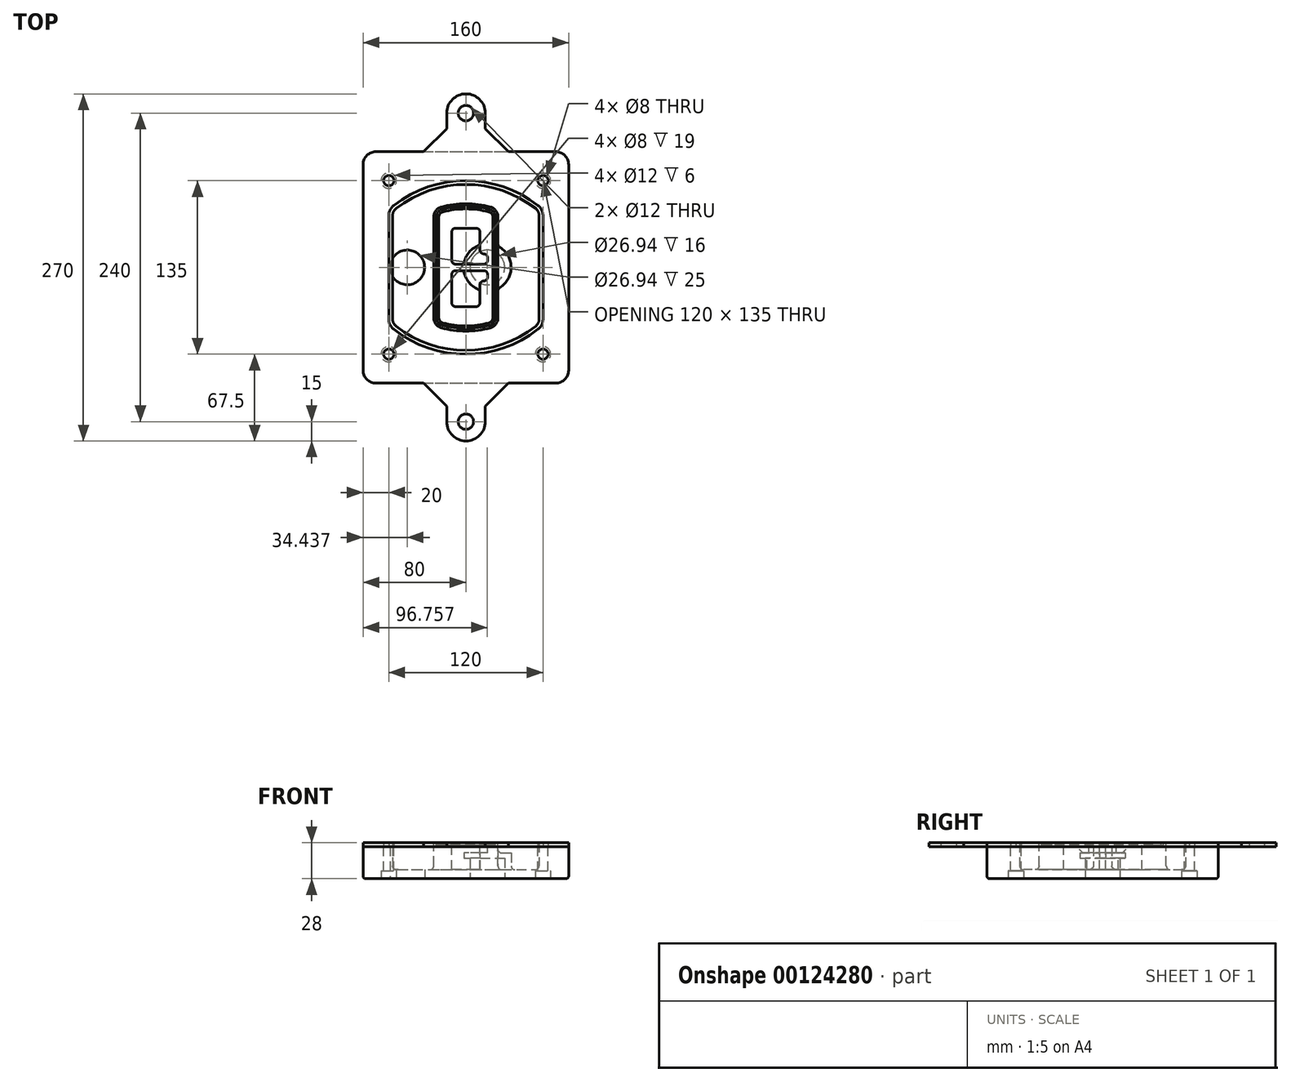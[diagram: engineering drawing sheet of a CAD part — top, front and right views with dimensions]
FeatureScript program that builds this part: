
annotation { "Feature Type Name" : "Feature", "Feature Type Description" : "" }
export const myFeature = defineFeature(function(context is Context, id is Id, definition is map)
    precondition{}
    {
        {
            var Q0;
            Q0=qCreatedBy(makeId("Top.planeOp"),FACE);
            var sketch = newSketch(context, id + "F0", { "sketchPlane" : qUnion([Q0])});
            skPoint(sketch, "E0.rect.middle", {"position": v(0, 0) * mm});
            skLineSegment(sketch, "E1.bottom", {"start": v(-70, -90) * mm, "end": v(70, -90) * mm});
            skLineSegment(sketch, "E1.top", {"start": v(-70, 90) * mm, "end": v(70, 90) * mm});
            skLineSegment(sketch, "E1.left", {"start": v(-80, -80) * mm, "end": v(-80, 80) * mm});
            skLineSegment(sketch, "E1.right", {"start": v(80, -80) * mm, "end": v(80, 80) * mm});
            skLineSegment(sketch, "E2", {"start": v(-80, 90) * mm, "end": v(80, -90) * mm, "construction": true});
            skLineSegment(sketch, "E3", {"start": v(80, 90) * mm, "end": v(-80, -90) * mm, "construction": true});
            skCircle(sketch, "E4", {"center": v(-60, 67.5) * mm, "radius": 4 * mm});
            skCircle(sketch, "E5", {"center": v(60, 67.5) * mm, "radius": 4 * mm});
            skCircle(sketch, "E6", {"center": v(60, -67.5) * mm, "radius": 4 * mm});
            skCircle(sketch, "E7", {"center": v(-60, -67.5) * mm, "radius": 4 * mm});
            skLineSegment(sketch, "E8", {"start": v(-60, 67.5) * mm, "end": v(60, 67.5) * mm, "construction": true});
            skLineSegment(sketch, "E9", {"start": v(60, 67.5) * mm, "end": v(60, -67.5) * mm, "construction": true});
            skLineSegment(sketch, "E10", {"start": v(60, -67.5) * mm, "end": v(-60, -67.5) * mm, "construction": true});
            skLineSegment(sketch, "E11", {"start": v(-60, -67.5) * mm, "end": v(-60, 67.5) * mm, "construction": true});
            skLineSegment(sketch, "E12", {"start": v(-60, 40.3) * mm, "end": v(-60, -40.3) * mm});
            skLineSegment(sketch, "E13", {"start": v(60, 40.3) * mm, "end": v(60, -40.3) * mm});
            skArc(sketch, "E14", {"start": v(56.15, 48.18) * mm, "mid": v(0, 67.5) * mm, "end": v(-56.15, 48.18) * mm});
            skArc(sketch, "E15", {"start": v(-56.15, -48.18) * mm, "mid": v(0, -67.5) * mm, "end": v(56.15, -48.18) * mm});
            skLineSegment(sketch, "E16", {"start": v(-60, 0) * mm, "end": v(60, 0) * mm, "construction": true});
            skPoint(sketch, "E17.visualSharp", {"position": v(-60, -45) * mm});
            skArc(sketch, "E17.filletArc", {"start": v(-60, -40.3) * mm, "mid": v(-58.99, -44.68) * mm, "end": v(-56.15, -48.18) * mm});
            skPoint(sketch, "E18.visualSharp", {"position": v(-60, 45) * mm});
            skArc(sketch, "E18.filletArc", {"start": v(-56.15, 48.18) * mm, "mid": v(-58.99, 44.68) * mm, "end": v(-60, 40.3) * mm});
            skPoint(sketch, "E19.visualSharp", {"position": v(60, 45) * mm});
            skArc(sketch, "E19.filletArc", {"start": v(60, 40.3) * mm, "mid": v(58.99, 44.68) * mm, "end": v(56.15, 48.18) * mm});
            skPoint(sketch, "E20.visualSharp", {"position": v(60, -45) * mm});
            skArc(sketch, "E20.filletArc", {"start": v(56.15, -48.18) * mm, "mid": v(58.99, -44.68) * mm, "end": v(60, -40.3) * mm});
            skPoint(sketch, "E21.visualSharp", {"position": v(-80, 90) * mm});
            skArc(sketch, "E21.filletArc", {"start": v(-70, 90) * mm, "mid": v(-77.07, 87.07) * mm, "end": v(-80, 80) * mm});
            skPoint(sketch, "E22.visualSharp", {"position": v(80, 90) * mm});
            skArc(sketch, "E22.filletArc", {"start": v(80, 80) * mm, "mid": v(77.07, 87.07) * mm, "end": v(70, 90) * mm});
            skPoint(sketch, "E23.visualSharp", {"position": v(80, -90) * mm});
            skArc(sketch, "E23.filletArc", {"start": v(70, -90) * mm, "mid": v(77.07, -87.07) * mm, "end": v(80, -80) * mm});
            skPoint(sketch, "E24.visualSharp", {"position": v(-80, -90) * mm});
            skArc(sketch, "E24.filletArc", {"start": v(-80, -80) * mm, "mid": v(-77.07, -87.07) * mm, "end": v(-70, -90) * mm});
            skArc(sketch, "E25.0", {"start": v(57, 40.3) * mm, "mid": v(56.3, 43.36) * mm, "end": v(54.3, 45.81) * mm});
            skLineSegment(sketch, "E25.1", {"start": v(57, 40.3) * mm, "end": v(57, -40.3) * mm});
            skArc(sketch, "E25.2", {"start": v(54.3, -45.81) * mm, "mid": v(56.3, -43.36) * mm, "end": v(57, -40.3) * mm});
            skArc(sketch, "E25.3", {"start": v(-54.3, -45.81) * mm, "mid": v(0, -64.5) * mm, "end": v(54.3, -45.81) * mm});
            skArc(sketch, "E25.4", {"start": v(-57, -40.3) * mm, "mid": v(-56.3, -43.36) * mm, "end": v(-54.3, -45.81) * mm});
            skArc(sketch, "E25.5", {"start": v(54.3, 45.81) * mm, "mid": v(0, 64.5) * mm, "end": v(-54.3, 45.81) * mm});
            skLineSegment(sketch, "E25.6", {"start": v(-57, 40.3) * mm, "end": v(-57, -40.3) * mm});
            skArc(sketch, "E25.7", {"start": v(-54.3, 45.81) * mm, "mid": v(-56.3, 43.36) * mm, "end": v(-57, 40.3) * mm});
            skArc(sketch, "E26.0", {"start": v(-58.62, 51.33) * mm, "mid": v(-62.58, 46.43) * mm, "end": v(-64, 40.3) * mm});
            skArc(sketch, "E26.1", {"start": v(58.62, 51.33) * mm, "mid": v(0, 71.5) * mm, "end": v(-58.62, 51.33) * mm});
            skArc(sketch, "E26.2", {"start": v(64, 40.3) * mm, "mid": v(62.58, 46.43) * mm, "end": v(58.62, 51.33) * mm});
            skLineSegment(sketch, "E26.3", {"start": v(64, 40.3) * mm, "end": v(64, -40.3) * mm});
            skArc(sketch, "E26.4", {"start": v(58.62, -51.33) * mm, "mid": v(62.58, -46.43) * mm, "end": v(64, -40.3) * mm});
            skLineSegment(sketch, "E26.5", {"start": v(-64, 40.3) * mm, "end": v(-64, -40.3) * mm});
            skArc(sketch, "E26.6", {"start": v(-58.62, -51.33) * mm, "mid": v(0, -71.5) * mm, "end": v(58.62, -51.33) * mm});
            skArc(sketch, "E26.7", {"start": v(-64, -40.3) * mm, "mid": v(-62.58, -46.43) * mm, "end": v(-58.62, -51.33) * mm});
            skSolve(sketch);
        }
        {
            var Q0;
            Q0=makeQuery(id+"F0.imprint","IMPRINT",FACE,{"disambiguationData":[TD([[makeQuery(id+"F0.imprint","IMPRINT",EDGE,{"derivedFrom":sQuery(id+"F0.wireOp",EDGE,"E1.bottom")}),1.0]])]});
            var Q1;
            Q1=makeQuery(id+"F0.imprint","IMPRINT",FACE,{"disambiguationData":[TD([[makeQuery(id+"F0.imprint","IMPRINT",EDGE,{"derivedFrom":sQuery(id+"F0.wireOp",EDGE,"E12")}),1.0]])]});
            var Q2;
            Q2=makeQuery(id+"F0.imprint","IMPRINT",FACE,{"disambiguationData":[TD([[makeQuery(id+"F0.imprint","IMPRINT",EDGE,{"derivedFrom":sQuery(id+"F0.wireOp",EDGE,"E25.0")}),1.0]])]});
            var Q3;
            Q3=makeQuery(id+"F0.imprint","IMPRINT",FACE,{"disambiguationData":[TD([[makeQuery(id+"F0.imprint","IMPRINT",EDGE,{"derivedFrom":sQuery(id+"F0.wireOp",EDGE,"E12")}),-1.0]])]});
            extrude(context, id + "F1", {"entities" : qUnion([Q0, Q1, Q2, Q3]), "oppositeDirection" : true, "depth" : 25 * mm});
        }
        {
            var Q0;
            Q0=makeQuery(id+"F0.imprint","IMPRINT",FACE,{"disambiguationData":[TD([[makeQuery(id+"F0.imprint","IMPRINT",EDGE,{"derivedFrom":sQuery(id+"F0.wireOp",EDGE,"E12")}),1.0]])]});
            extrude(context, id + "F2", {"entities" : qUnion([Q0]), "operationType" : NewBodyOperationType.ADD, "depth" : 3 * mm});
        }
        {
            var Q0;
            Q0=makeQuery(id+"F0.imprint","IMPRINT",FACE,{"disambiguationData":[TD([[makeQuery(id+"F0.imprint","IMPRINT",EDGE,{"derivedFrom":sQuery(id+"F0.wireOp",EDGE,"E25.0")}),1.0]])]});
            extrude(context, id + "F3", {"entities" : qUnion([Q0]), "operationType" : NewBodyOperationType.REMOVE, "oppositeDirection" : true, "depth" : 18 * mm});
        }
        {
            var Q0;
            Q0=makeQuery(id+"F2.opExtrude","CAP_FACE",FACE,{"disambiguationData":[OSD([sQuery(id+"F0.wireOp",EDGE,"E12"),sQuery(id+"F0.wireOp",EDGE,"E13"),sQuery(id+"F0.wireOp",EDGE,"E14"),sQuery(id+"F0.wireOp",EDGE,"E15"),sQuery(id+"F0.wireOp",EDGE,"E17.filletArc"),sQuery(id+"F0.wireOp",EDGE,"E18.filletArc"),sQuery(id+"F0.wireOp",EDGE,"E19.filletArc"),sQuery(id+"F0.wireOp",EDGE,"E20.filletArc"),sQuery(id+"F0.wireOp",EDGE,"E25.0"),sQuery(id+"F0.wireOp",EDGE,"E25.1"),sQuery(id+"F0.wireOp",EDGE,"E25.2"),sQuery(id+"F0.wireOp",EDGE,"E25.3"),sQuery(id+"F0.wireOp",EDGE,"E25.4"),sQuery(id+"F0.wireOp",EDGE,"E25.5"),sQuery(id+"F0.wireOp",EDGE,"E25.6"),sQuery(id+"F0.wireOp",EDGE,"E25.7")])],"isStart":false});
            var sketch = newSketch(context, id + "F4", { "sketchPlane" : qUnion([Q0])});
            skArc(sketch, "E27.0", {"start": v(-19.08, -46.97) * mm, "mid": v(0, -49.5) * mm, "end": v(19.08, -46.97) * mm});
            skArc(sketch, "E28.0", {"start": v(19.08, 46.97) * mm, "mid": v(0, 49.5) * mm, "end": v(-19.08, 46.97) * mm});
            skLineSegment(sketch, "E29", {"start": v(-25, 39.25) * mm, "end": v(-25, -39.25) * mm});
            skLineSegment(sketch, "E30", {"start": v(25, 39.25) * mm, "end": v(25, -39.25) * mm});
            skLineSegment(sketch, "E31", {"start": v(-25, 45.1) * mm, "end": v(25, 45.1) * mm, "construction": true});
            skLineSegment(sketch, "E32", {"start": v(-25, -45.1) * mm, "end": v(25, -45.1) * mm, "construction": true});
            skPoint(sketch, "E33.visualSharp", {"position": v(-25, 45.1) * mm});
            skArc(sketch, "E33.filletArc", {"start": v(-19.08, 46.97) * mm, "mid": v(-23.35, 44.11) * mm, "end": v(-25, 39.25) * mm});
            skPoint(sketch, "E34.visualSharp", {"position": v(25, 45.1) * mm});
            skArc(sketch, "E34.filletArc", {"start": v(25, 39.25) * mm, "mid": v(23.35, 44.11) * mm, "end": v(19.08, 46.97) * mm});
            skPoint(sketch, "E35.visualSharp", {"position": v(25, -45.1) * mm});
            skArc(sketch, "E35.filletArc", {"start": v(19.08, -46.97) * mm, "mid": v(23.35, -44.11) * mm, "end": v(25, -39.25) * mm});
            skPoint(sketch, "E36.visualSharp", {"position": v(-25, -45.1) * mm});
            skArc(sketch, "E36.filletArc", {"start": v(-25, -39.25) * mm, "mid": v(-23.35, -44.11) * mm, "end": v(-19.08, -46.97) * mm});
            skArc(sketch, "E37.0", {"start": v(54.3, 45.81) * mm, "mid": v(0, 64.5) * mm, "end": v(-54.3, 45.81) * mm});
            skArc(sketch, "E37.1", {"start": v(-54.3, 45.81) * mm, "mid": v(-56.3, 43.36) * mm, "end": v(-57, 40.3) * mm});
            skLineSegment(sketch, "E37.2", {"start": v(-57, 40.3) * mm, "end": v(-57, -40.3) * mm});
            skArc(sketch, "E37.3", {"start": v(-57, -40.3) * mm, "mid": v(-56.3, -43.36) * mm, "end": v(-54.3, -45.81) * mm});
            skArc(sketch, "E37.4", {"start": v(-54.3, -45.81) * mm, "mid": v(0, -64.5) * mm, "end": v(54.3, -45.81) * mm});
            skArc(sketch, "E37.5", {"start": v(54.3, -45.81) * mm, "mid": v(56.3, -43.36) * mm, "end": v(57, -40.3) * mm});
            skLineSegment(sketch, "E37.6", {"start": v(57, 40.3) * mm, "end": v(57, -40.3) * mm});
            skArc(sketch, "E37.7", {"start": v(57, 40.3) * mm, "mid": v(56.3, 43.36) * mm, "end": v(54.3, 45.81) * mm});
            skLineSegment(sketch, "E38.0", {"start": v(23, 39.25) * mm, "end": v(23, -39.25) * mm});
            skArc(sketch, "E38.1", {"start": v(18.56, -45.04) * mm, "mid": v(21.76, -42.9) * mm, "end": v(23, -39.25) * mm});
            skArc(sketch, "E38.2", {"start": v(-18.56, -45.04) * mm, "mid": v(0, -47.5) * mm, "end": v(18.56, -45.04) * mm});
            skArc(sketch, "E38.3", {"start": v(-23, -39.25) * mm, "mid": v(-21.76, -42.9) * mm, "end": v(-18.56, -45.04) * mm});
            skLineSegment(sketch, "E38.4", {"start": v(-23, 39.25) * mm, "end": v(-23, -39.25) * mm});
            skArc(sketch, "E38.5", {"start": v(23, 39.25) * mm, "mid": v(21.76, 42.9) * mm, "end": v(18.56, 45.04) * mm});
            skArc(sketch, "E38.6", {"start": v(-18.56, 45.04) * mm, "mid": v(-21.76, 42.9) * mm, "end": v(-23, 39.25) * mm});
            skArc(sketch, "E38.7", {"start": v(18.56, 45.04) * mm, "mid": v(0, 47.5) * mm, "end": v(-18.56, 45.04) * mm});
            skArc(sketch, "E39.0", {"start": v(21, 39.25) * mm, "mid": v(20.18, 41.68) * mm, "end": v(18.04, 43.1) * mm});
            skLineSegment(sketch, "E39.1", {"start": v(21, 39.25) * mm, "end": v(21, -39.25) * mm});
            skArc(sketch, "E39.2", {"start": v(18.04, -43.1) * mm, "mid": v(20.18, -41.68) * mm, "end": v(21, -39.25) * mm});
            skArc(sketch, "E39.3", {"start": v(-18.04, -43.1) * mm, "mid": v(0, -45.5) * mm, "end": v(18.04, -43.1) * mm});
            skArc(sketch, "E39.4", {"start": v(-21, -39.25) * mm, "mid": v(-20.18, -41.68) * mm, "end": v(-18.04, -43.1) * mm});
            skArc(sketch, "E39.5", {"start": v(18.04, 43.1) * mm, "mid": v(0, 45.5) * mm, "end": v(-18.04, 43.1) * mm});
            skLineSegment(sketch, "E39.6", {"start": v(-21, 39.25) * mm, "end": v(-21, -39.25) * mm});
            skArc(sketch, "E39.7", {"start": v(-18.04, 43.1) * mm, "mid": v(-20.18, 41.68) * mm, "end": v(-21, 39.25) * mm});
            skLineSegment(sketch, "E40", {"start": v(-25, 0) * mm, "end": v(25, 0) * mm, "construction": true});
            skLineSegment(sketch, "E41", {"start": v(-11, 5.5) * mm, "end": v(-11, 27.5) * mm});
            skLineSegment(sketch, "E42", {"start": v(-8, 30.5) * mm, "end": v(8, 30.5) * mm});
            skLineSegment(sketch, "E43", {"start": v(11, 27.5) * mm, "end": v(11, 13.5) * mm});
            skLineSegment(sketch, "E44", {"start": v(14, 10.5) * mm, "end": v(14, 10.5) * mm});
            skLineSegment(sketch, "E45", {"start": v(17, 7.5) * mm, "end": v(17, 5.5) * mm});
            skLineSegment(sketch, "E46", {"start": v(14, 2.5) * mm, "end": v(-8, 2.5) * mm});
            skPoint(sketch, "E47.visualSharp", {"position": v(-11, 30.5) * mm});
            skArc(sketch, "E47.filletArc", {"start": v(-8, 30.5) * mm, "mid": v(-10.12, 29.62) * mm, "end": v(-11, 27.5) * mm});
            skPoint(sketch, "E48.visualSharp", {"position": v(11, 30.5) * mm});
            skArc(sketch, "E48.filletArc", {"start": v(11, 27.5) * mm, "mid": v(10.12, 29.62) * mm, "end": v(8, 30.5) * mm});
            skPoint(sketch, "E49.visualSharp", {"position": v(11, 10.5) * mm});
            skArc(sketch, "E49.filletArc", {"start": v(11, 13.5) * mm, "mid": v(11.88, 11.38) * mm, "end": v(14, 10.5) * mm});
            skPoint(sketch, "E50.visualSharp", {"position": v(17, 10.5) * mm});
            skArc(sketch, "E50.filletArc", {"start": v(17, 7.5) * mm, "mid": v(16.12, 9.62) * mm, "end": v(14, 10.5) * mm});
            skPoint(sketch, "E51.visualSharp", {"position": v(17, 2.5) * mm});
            skArc(sketch, "E51.filletArc", {"start": v(14, 2.5) * mm, "mid": v(16.12, 3.38) * mm, "end": v(17, 5.5) * mm});
            skPoint(sketch, "E52.visualSharp", {"position": v(-11, 2.5) * mm});
            skArc(sketch, "E52.filletArc", {"start": v(-11, 5.5) * mm, "mid": v(-10.12, 3.38) * mm, "end": v(-8, 2.5) * mm});
            skLineSegment(sketch, "E53.0.MirrorCS", {"start": v(14, -2.5) * mm, "end": v(-8, -2.5) * mm});
            skArc(sketch, "E54.0.MirrorCS", {"start": v(-11, -5.5) * mm, "mid": v(-10.12, -3.38) * mm, "end": v(-8, -2.5) * mm});
            skLineSegment(sketch, "E55.0.MirrorCS", {"start": v(-11, -5.5) * mm, "end": v(-11, -27.5) * mm});
            skArc(sketch, "E56.0.MirrorCS", {"start": v(-8, -30.5) * mm, "mid": v(-10.12, -29.62) * mm, "end": v(-11, -27.5) * mm});
            skLineSegment(sketch, "E57.0.MirrorCS", {"start": v(-8, -30.5) * mm, "end": v(8, -30.5) * mm});
            skArc(sketch, "E58.0.MirrorCS", {"start": v(11, -27.5) * mm, "mid": v(10.12, -29.62) * mm, "end": v(8, -30.5) * mm});
            skLineSegment(sketch, "E59.0.MirrorCS", {"start": v(11, -27.5) * mm, "end": v(11, -13.5) * mm});
            skArc(sketch, "E60.0.MirrorCS", {"start": v(11, -13.5) * mm, "mid": v(11.88, -11.38) * mm, "end": v(14, -10.5) * mm});
            skArc(sketch, "E61.0.MirrorCS", {"start": v(17, -7.5) * mm, "mid": v(16.12, -9.62) * mm, "end": v(14, -10.5) * mm});
            skLineSegment(sketch, "E62.0.MirrorCS", {"start": v(17, -7.5) * mm, "end": v(17, -5.5) * mm});
            skArc(sketch, "E63.0.MirrorCS", {"start": v(14, -2.5) * mm, "mid": v(16.12, -3.38) * mm, "end": v(17, -5.5) * mm});
            skSolve(sketch);
        }
        {
            var Q0;
            Q0=makeQuery(id+"F4.imprint","IMPRINT",FACE,{"disambiguationData":[TD([[makeQuery(id+"F4.imprint","IMPRINT",EDGE,{"derivedFrom":sQuery(id+"F4.wireOp",EDGE,"E27.0")}),1.0]])]});
            var Q1;
            Q1=makeQuery(id+"F4.imprint","IMPRINT",FACE,{"disambiguationData":[TD([[makeQuery(id+"F4.imprint","IMPRINT",EDGE,{"derivedFrom":sQuery(id+"F4.wireOp",EDGE,"E38.0")}),-1.0]])]});
            var Q2;
            Q2=makeQuery(id+"F4.imprint","IMPRINT",FACE,{"disambiguationData":[TD([[makeQuery(id+"F4.imprint","IMPRINT",EDGE,{"derivedFrom":sQuery(id+"F4.wireOp",EDGE,"E39.0")}),1.0]])]});
            extrude(context, id + "F5", {"entities" : qUnion([Q0, Q1, Q2]), "operationType" : NewBodyOperationType.ADD, "endBound" : BoundingType.UP_TO_NEXT, "oppositeDirection" : true, "depth" : 25 * mm});
        }
        {
            var Q0;
            Q0=makeQuery(id+"F4.imprint","IMPRINT",FACE,{"disambiguationData":[TD([[makeQuery(id+"F4.imprint","IMPRINT",EDGE,{"derivedFrom":sQuery(id+"F4.wireOp",EDGE,"E38.0")}),-1.0]])]});
            extrude(context, id + "F6", {"entities" : qUnion([Q0]), "operationType" : NewBodyOperationType.REMOVE, "oppositeDirection" : true, "depth" : 2 * mm});
        }
        {
            var Q0;
            Q0=makeQuery(id+"F1.opExtrude","CAP_FACE",FACE,{"disambiguationData":[OSD([sQuery(id+"F0.wireOp",EDGE,"E1.bottom"),sQuery(id+"F0.wireOp",EDGE,"E1.top"),sQuery(id+"F0.wireOp",EDGE,"E1.left"),sQuery(id+"F0.wireOp",EDGE,"E1.right"),sQuery(id+"F0.wireOp",EDGE,"E4"),sQuery(id+"F0.wireOp",EDGE,"E5"),sQuery(id+"F0.wireOp",EDGE,"E6"),sQuery(id+"F0.wireOp",EDGE,"E7"),sQuery(id+"F0.wireOp",EDGE,"E21.filletArc"),sQuery(id+"F0.wireOp",EDGE,"E22.filletArc"),sQuery(id+"F0.wireOp",EDGE,"E23.filletArc"),sQuery(id+"F0.wireOp",EDGE,"E24.filletArc")])],"isStart":false});
            var sketch = newSketch(context, id + "F7", { "sketchPlane" : qUnion([Q0])});
            skCircle(sketch, "E64", {"center": v(16.76, 0) * mm, "radius": 13.47 * mm});
            skCircle(sketch, "E65", {"center": v(-45.56, 0) * mm, "radius": 13.47 * mm});
            skLineSegment(sketch, "E66", {"start": v(80, 0) * mm, "end": v(-80, 0) * mm});
            skCircle(sketch, "E67", {"center": v(16.76, 0) * mm, "radius": 18.47 * mm});
            skCircle(sketch, "E68", {"center": v(60, -67.5) * mm, "radius": 6 * mm});
            skCircle(sketch, "E69", {"center": v(-60, -67.5) * mm, "radius": 6 * mm});
            skCircle(sketch, "E70", {"center": v(-60, 67.5) * mm, "radius": 6 * mm});
            skCircle(sketch, "E71", {"center": v(60, 67.5) * mm, "radius": 6 * mm});
            skSolve(sketch);
        }
        {
            var Q0;
            {var subQ1=sQuery(id+"F7.wireOp",EDGE,"E66");var subQ4=sQuery(id+"F7.wireOp",EDGE,"E64");var subQ6=makeQuery(id+"F7.imprint","INTERSECT",VERTEX,{"disambiguationData":[OD(0.0)],"derivedFrom":[subQ4,subQ1]});Q0=makeQuery(id+"F7.imprint","IMPRINT",FACE,{"disambiguationData":[TD([[makeQuery(id+"F7.imprint","IMPRINT",EDGE,{"disambiguationData":[TD([[subQ6,-1.0]])],"derivedFrom":subQ4}),-1.0]])]});}
            var Q1;
            {var subQ0=sQuery(id+"F7.wireOp",EDGE,"E66");var subQ1=sQuery(id+"F7.wireOp",EDGE,"E64");var subQ3=makeQuery(id+"F7.imprint","INTERSECT",VERTEX,{"disambiguationData":[OD(0.0)],"derivedFrom":[subQ1,subQ0]});Q1=makeQuery(id+"F7.imprint","IMPRINT",FACE,{"disambiguationData":[TD([[makeQuery(id+"F7.imprint","IMPRINT",EDGE,{"disambiguationData":[TD([[subQ3,-1.0]])],"derivedFrom":subQ1}),1.0]])]});}
            var Q2;
            {var subQ0=sQuery(id+"F7.wireOp",EDGE,"E66");var subQ1=sQuery(id+"F7.wireOp",EDGE,"E64");var subQ3=makeQuery(id+"F7.imprint","INTERSECT",VERTEX,{"disambiguationData":[OD(0.0)],"derivedFrom":[subQ1,subQ0]});Q2=makeQuery(id+"F7.imprint","IMPRINT",FACE,{"disambiguationData":[TD([[makeQuery(id+"F7.imprint","IMPRINT",EDGE,{"disambiguationData":[TD([[subQ3,1.0]])],"derivedFrom":subQ1}),1.0]])]});}
            var Q3;
            {var subQ1=sQuery(id+"F7.wireOp",EDGE,"E66");var subQ4=sQuery(id+"F7.wireOp",EDGE,"E64");var subQ6=makeQuery(id+"F7.imprint","INTERSECT",VERTEX,{"disambiguationData":[OD(0.0)],"derivedFrom":[subQ4,subQ1]});Q3=makeQuery(id+"F7.imprint","IMPRINT",FACE,{"disambiguationData":[TD([[makeQuery(id+"F7.imprint","IMPRINT",EDGE,{"disambiguationData":[TD([[subQ6,1.0]])],"derivedFrom":subQ4}),-1.0]])]});}
            extrude(context, id + "F8", {"entities" : qUnion([Q0, Q1, Q2, Q3]), "operationType" : NewBodyOperationType.ADD, "oppositeDirection" : true, "depth" : 20 * mm});
        }
        {
            var Q0;
            {var subQ0=sQuery(id+"F7.wireOp",EDGE,"E66");var subQ1=sQuery(id+"F7.wireOp",EDGE,"E64");var subQ3=makeQuery(id+"F7.imprint","INTERSECT",VERTEX,{"disambiguationData":[OD(0.0)],"derivedFrom":[subQ1,subQ0]});Q0=makeQuery(id+"F7.imprint","IMPRINT",FACE,{"disambiguationData":[TD([[makeQuery(id+"F7.imprint","IMPRINT",EDGE,{"disambiguationData":[TD([[subQ3,-1.0]])],"derivedFrom":subQ1}),1.0]])]});}
            var Q1;
            {var subQ0=sQuery(id+"F7.wireOp",EDGE,"E66");var subQ1=sQuery(id+"F7.wireOp",EDGE,"E64");var subQ3=makeQuery(id+"F7.imprint","INTERSECT",VERTEX,{"disambiguationData":[OD(0.0)],"derivedFrom":[subQ1,subQ0]});Q1=makeQuery(id+"F7.imprint","IMPRINT",FACE,{"disambiguationData":[TD([[makeQuery(id+"F7.imprint","IMPRINT",EDGE,{"disambiguationData":[TD([[subQ3,1.0]])],"derivedFrom":subQ1}),1.0]])]});}
            extrude(context, id + "F9", {"entities" : qUnion([Q0, Q1]), "operationType" : NewBodyOperationType.REMOVE, "oppositeDirection" : true, "depth" : 16 * mm});
        }
        {
            var Q0;
            {var subQ0=sQuery(id+"F7.wireOp",EDGE,"E66");var subQ1=sQuery(id+"F7.wireOp",EDGE,"E65");var subQ3=makeQuery(id+"F7.imprint","INTERSECT",VERTEX,{"disambiguationData":[OD(0.0)],"derivedFrom":[subQ1,subQ0]});Q0=makeQuery(id+"F7.imprint","IMPRINT",FACE,{"disambiguationData":[TD([[makeQuery(id+"F7.imprint","IMPRINT",EDGE,{"disambiguationData":[TD([[subQ3,-1.0]])],"derivedFrom":subQ1}),1.0]])]});}
            var Q1;
            {var subQ0=sQuery(id+"F7.wireOp",EDGE,"E66");var subQ1=sQuery(id+"F7.wireOp",EDGE,"E65");var subQ3=makeQuery(id+"F7.imprint","INTERSECT",VERTEX,{"disambiguationData":[OD(0.0)],"derivedFrom":[subQ1,subQ0]});Q1=makeQuery(id+"F7.imprint","IMPRINT",FACE,{"disambiguationData":[TD([[makeQuery(id+"F7.imprint","IMPRINT",EDGE,{"disambiguationData":[TD([[subQ3,1.0]])],"derivedFrom":subQ1}),1.0]])]});}
            extrude(context, id + "F10", {"entities" : qUnion([Q0, Q1]), "operationType" : NewBodyOperationType.REMOVE, "oppositeDirection" : true, "depth" : 25 * mm});
        }
        {
            var Q0;
            Q0=makeQuery(id+"F7.imprint","IMPRINT",FACE,{"disambiguationData":[TD([[makeQuery(id+"F7.imprint","IMPRINT",EDGE,{"derivedFrom":sQuery(id+"F7.wireOp",EDGE,"E68")}),1.0]])]});
            var Q1;
            Q1=makeQuery(id+"F7.imprint","IMPRINT",FACE,{"disambiguationData":[TD([[makeQuery(id+"F7.imprint","IMPRINT",EDGE,{"derivedFrom":makeQuery(id+"F1.opExtrude","CAP_EDGE",EDGE,{"disambiguationData":[OSD([sQuery(id+"F0.wireOp",EDGE,"E5")])],"isStart":false})}),-1.0]])]});
            var Q2;
            Q2=makeQuery(id+"F7.imprint","IMPRINT",FACE,{"disambiguationData":[TD([[makeQuery(id+"F7.imprint","IMPRINT",EDGE,{"derivedFrom":sQuery(id+"F7.wireOp",EDGE,"E69")}),1.0]])]});
            var Q3;
            Q3=makeQuery(id+"F7.imprint","IMPRINT",FACE,{"disambiguationData":[TD([[makeQuery(id+"F7.imprint","IMPRINT",EDGE,{"derivedFrom":makeQuery(id+"F1.opExtrude","CAP_EDGE",EDGE,{"disambiguationData":[OSD([sQuery(id+"F0.wireOp",EDGE,"E4")])],"isStart":false})}),-1.0]])]});
            var Q4;
            Q4=makeQuery(id+"F7.imprint","IMPRINT",FACE,{"disambiguationData":[TD([[makeQuery(id+"F7.imprint","IMPRINT",EDGE,{"derivedFrom":sQuery(id+"F7.wireOp",EDGE,"E70")}),1.0]])]});
            var Q5;
            Q5=makeQuery(id+"F7.imprint","IMPRINT",FACE,{"disambiguationData":[TD([[makeQuery(id+"F7.imprint","IMPRINT",EDGE,{"derivedFrom":makeQuery(id+"F1.opExtrude","CAP_EDGE",EDGE,{"disambiguationData":[OSD([sQuery(id+"F0.wireOp",EDGE,"E7")])],"isStart":false})}),-1.0]])]});
            var Q6;
            Q6=makeQuery(id+"F7.imprint","IMPRINT",FACE,{"disambiguationData":[TD([[makeQuery(id+"F7.imprint","IMPRINT",EDGE,{"derivedFrom":sQuery(id+"F7.wireOp",EDGE,"E71")}),1.0]])]});
            var Q7;
            Q7=makeQuery(id+"F7.imprint","IMPRINT",FACE,{"disambiguationData":[TD([[makeQuery(id+"F7.imprint","IMPRINT",EDGE,{"derivedFrom":makeQuery(id+"F1.opExtrude","CAP_EDGE",EDGE,{"disambiguationData":[OSD([sQuery(id+"F0.wireOp",EDGE,"E6")])],"isStart":false})}),-1.0]])]});
            extrude(context, id + "F11", {"entities" : qUnion([Q0, Q1, Q2, Q3, Q4, Q5, Q6, Q7]), "operationType" : NewBodyOperationType.REMOVE, "oppositeDirection" : true, "depth" : 6 * mm});
        }
        {
            var Q0;
            Q0=makeQuery(id+"F9.boolean.opBoolean","COPY",FACE,{"derivedFrom":makeQuery(id+"F9.opExtrude","CAP_FACE",FACE,{"disambiguationData":[OSD([sQuery(id+"F7.wireOp",EDGE,"E64")])],"isStart":false})});
            var sketch = newSketch(context, id + "F12", { "sketchPlane" : qUnion([Q0])});
            skArc(sketch, "E72.0", {"start": v(11, 17.55) * mm, "mid": v(2.57, 11.82) * mm, "end": v(-1.54, 2.5) * mm});
            skArc(sketch, "E72.1", {"start": v(-1.54, -2.5) * mm, "mid": v(2.57, -11.82) * mm, "end": v(11, -17.55) * mm});
            skLineSegment(sketch, "E73", {"start": v(-1.54, -2.5) * mm, "end": v(14, -2.5) * mm});
            skLineSegment(sketch, "E74.0", {"start": v(14, 2.5) * mm, "end": v(-1.54, 2.5) * mm});
            skArc(sketch, "E74.1", {"start": v(14, 2.5) * mm, "mid": v(16.12, 3.38) * mm, "end": v(17, 5.5) * mm});
            skLineSegment(sketch, "E74.2", {"start": v(17, 7.5) * mm, "end": v(17, 5.5) * mm});
            skArc(sketch, "E74.3", {"start": v(17, 7.5) * mm, "mid": v(16.12, 9.62) * mm, "end": v(14, 10.5) * mm});
            skArc(sketch, "E74.4", {"start": v(11, 13.5) * mm, "mid": v(11.88, 11.38) * mm, "end": v(14, 10.5) * mm});
            skLineSegment(sketch, "E74.5", {"start": v(11, 17.55) * mm, "end": v(11, 13.5) * mm});
            skLineSegment(sketch, "E74.7", {"start": v(14, -2.5) * mm, "end": v(-1.54, -2.5) * mm});
            skArc(sketch, "E74.8", {"start": v(14, -2.5) * mm, "mid": v(16.12, -3.38) * mm, "end": v(17, -5.5) * mm});
            skLineSegment(sketch, "E74.9", {"start": v(17, -7.5) * mm, "end": v(17, -5.5) * mm});
            skArc(sketch, "E74.10", {"start": v(17, -7.5) * mm, "mid": v(16.12, -9.62) * mm, "end": v(14, -10.5) * mm});
            skArc(sketch, "E74.11", {"start": v(11, -13.5) * mm, "mid": v(11.88, -11.38) * mm, "end": v(14, -10.5) * mm});
            skLineSegment(sketch, "E74.12", {"start": v(11, -17.55) * mm, "end": v(11, -13.5) * mm});
            skPoint(sketch, "E75.orphan", {"position": v(11, -27.5) * mm});
            skPoint(sketch, "E76.orphan", {"position": v(-8, -2.5) * mm});
            skPoint(sketch, "E77.orphan", {"position": v(-8, 2.5) * mm});
            skPoint(sketch, "E78.orphan", {"position": v(11, 27.5) * mm});
            skSolve(sketch);
        }
        {
            var Q0;
            {var subQ7=sQuery(id+"F12.wireOp",EDGE,"E72.0");var subQ14=sQuery(id+"F12.wireOp",EDGE,"E72.1");var subQ16=sQuery(id+"F12.wireOp",EDGE,"E74.1");var subQ18=sQuery(id+"F12.wireOp",EDGE,"E74.8");Q0=qUnion([makeQuery(id+"F12.imprint","IMPRINT",FACE,{"disambiguationData":[TD([[makeQuery(id+"F12.imprint","IMPRINT",EDGE,{"derivedFrom":subQ7}),1.0]])]}),makeQuery(id+"F12.imprint","IMPRINT",FACE,{"disambiguationData":[TD([[makeQuery(id+"F12.imprint","IMPRINT",EDGE,{"derivedFrom":subQ14}),1.0]])]}),makeQuery(id+"F12.imprint","IMPRINT",FACE,{"disambiguationData":[TD([[makeQuery(id+"F12.imprint","IMPRINT",EDGE,{"derivedFrom":subQ16}),1.0]])]}),makeQuery(id+"F12.imprint","IMPRINT",FACE,{"disambiguationData":[TD([[makeQuery(id+"F12.imprint","IMPRINT",EDGE,{"derivedFrom":subQ18}),-1.0]])]})]);}
            var Q1;
            Q1=makeQuery(id+"F5.boolean.opBoolean","SPLIT",FACE,{"disambiguationData":[TD([makeQuery(id+"F5.opExtrude","SWEPT_FACE",FACE,{"disambiguationData":[OSD([sQuery(id+"F4.wireOp",EDGE,"E41")])]})])],"derivedFrom":makeQuery(id+"F3.boolean.opBoolean","COPY",FACE,{"derivedFrom":makeQuery(id+"F3.opExtrude","CAP_FACE",FACE,{"disambiguationData":[OSD([sQuery(id+"F0.wireOp",EDGE,"E25.0"),sQuery(id+"F0.wireOp",EDGE,"E25.1"),sQuery(id+"F0.wireOp",EDGE,"E25.2"),sQuery(id+"F0.wireOp",EDGE,"E25.3"),sQuery(id+"F0.wireOp",EDGE,"E25.4"),sQuery(id+"F0.wireOp",EDGE,"E25.5"),sQuery(id+"F0.wireOp",EDGE,"E25.6"),sQuery(id+"F0.wireOp",EDGE,"E25.7")])],"isStart":false})})});
            extrude(context, id + "F13", {"entities" : qUnion([Q0]), "operationType" : NewBodyOperationType.REMOVE, "endBound" : BoundingType.UP_TO_SURFACE, "endBoundEntityFace" : qUnion([Q1]), "depth" : 25 * mm});
        }
        {
            var Q0;
            Q0=makeQuery(id+"F3.boolean.opBoolean","COPY",EDGE,{"derivedFrom":makeQuery(id+"F3.opExtrude","CAP_EDGE",EDGE,{"disambiguationData":[OSD([sQuery(id+"F0.wireOp",EDGE,"E25.6")])],"isStart":false})});
            var Q1;
            Q1=makeQuery(id+"F8.boolean.opBoolean","INTERSECT",EDGE,{"derivedFrom":[makeQuery(id+"F5.opExtrude","SWEPT_FACE",FACE,{"disambiguationData":[OSD([sQuery(id+"F4.wireOp",EDGE,"E30")])]}),makeQuery(id+"F8.opExtrude","CAP_FACE",FACE,{"disambiguationData":[OSD([sQuery(id+"F7.wireOp",EDGE,"E67")])],"isStart":false})]});
            var Q2;
            Q2=makeQuery(id+"F8.boolean.opBoolean","INTERSECT",EDGE,{"disambiguationData":[OD(1.0)],"derivedFrom":[makeQuery(id+"F5.opExtrude","SWEPT_FACE",FACE,{"disambiguationData":[OSD([sQuery(id+"F4.wireOp",EDGE,"E30")])]}),makeQuery(id+"F8.opExtrude","SWEPT_FACE",FACE,{"disambiguationData":[OSD([sQuery(id+"F7.wireOp",EDGE,"E67")])]})]});
            var Q3;
            {var subQ0=sQuery(id+"F4.wireOp",EDGE,"E30");Q3=makeQuery(id+"F8.boolean.opBoolean","SPLIT",EDGE,{"disambiguationData":[TD([makeQuery(id+"F5.opExtrude","SWEPT_FACE",FACE,{"disambiguationData":[OSD([sQuery(id+"F4.wireOp",EDGE,"E35.filletArc")])]})])],"derivedFrom":makeQuery(id+"F5.opExtrude","CAP_EDGE",EDGE,{"disambiguationData":[OSD([subQ0])],"isStart":false})});}
            var Q4;
            {var subQ0=sQuery(id+"F0.wireOp",EDGE,"E25.7");var subQ1=sQuery(id+"F0.wireOp",EDGE,"E25.1");var subQ2=sQuery(id+"F0.wireOp",EDGE,"E25.6");var subQ3=sQuery(id+"F0.wireOp",EDGE,"E25.5");var subQ4=sQuery(id+"F0.wireOp",EDGE,"E25.4");var subQ5=sQuery(id+"F0.wireOp",EDGE,"E25.0");var subQ6=sQuery(id+"F0.wireOp",EDGE,"E25.2");var subQ7=sQuery(id+"F0.wireOp",EDGE,"E25.3");Q4=makeQuery(id+"F8.boolean.opBoolean","INTERSECT",EDGE,{"derivedFrom":[makeQuery(id+"F5.boolean.opBoolean","SPLIT",FACE,{"disambiguationData":[TD([makeQuery(id+"F2.opExtrude","SWEPT_FACE",FACE,{"disambiguationData":[OSD([subQ5])]})])],"derivedFrom":makeQuery(id+"F3.boolean.opBoolean","COPY",FACE,{"derivedFrom":makeQuery(id+"F3.opExtrude","CAP_FACE",FACE,{"disambiguationData":[OSD([subQ5,subQ1,subQ6,subQ7,subQ4,subQ3,subQ2,subQ0])],"isStart":false})})}),makeQuery(id+"F8.opExtrude","SWEPT_FACE",FACE,{"disambiguationData":[OSD([sQuery(id+"F7.wireOp",EDGE,"E67")])]})]});}
            var Q5;
            Q5=makeQuery(id+"F8.boolean.opBoolean","INTERSECT",EDGE,{"disambiguationData":[OD(0.0)],"derivedFrom":[makeQuery(id+"F5.opExtrude","SWEPT_FACE",FACE,{"disambiguationData":[OSD([sQuery(id+"F4.wireOp",EDGE,"E30")])]}),makeQuery(id+"F8.opExtrude","SWEPT_FACE",FACE,{"disambiguationData":[OSD([sQuery(id+"F7.wireOp",EDGE,"E67")])]})]});
            fillet(context, id + "F14", {"entities" : qUnion([Q0, Q1, Q2, Q3, Q4, Q5]), "radius" : 3 * mm, "tangentPropagation" : true, "allowEdgeOverflow" : false});
        }
        {
            var Q0;
            Q0=makeQuery(id+"F1.opExtrude","CAP_EDGE",EDGE,{"disambiguationData":[OSD([sQuery(id+"F0.wireOp",EDGE,"E1.bottom")])],"isStart":false});
            fillet(context, id + "F15", {"entities" : qUnion([Q0]), "radius" : 2 * mm, "tangentPropagation" : true, "allowEdgeOverflow" : false});
        }
        {
            var Q0;
            {var subQ0=sQuery(id+"F0.wireOp",EDGE,"E22.filletArc");var subQ1=sQuery(id+"F0.wireOp",EDGE,"E7");var subQ2=sQuery(id+"F0.wireOp",EDGE,"E6");var subQ3=sQuery(id+"F0.wireOp",EDGE,"E5");var subQ4=sQuery(id+"F0.wireOp",EDGE,"E4");var subQ5=sQuery(id+"F0.wireOp",EDGE,"E1.bottom");var subQ6=sQuery(id+"F0.wireOp",EDGE,"E21.filletArc");var subQ7=sQuery(id+"F0.wireOp",EDGE,"E1.top");var subQ8=sQuery(id+"F0.wireOp",EDGE,"E1.left");var subQ9=sQuery(id+"F0.wireOp",EDGE,"E1.right");var subQ10=sQuery(id+"F0.wireOp",EDGE,"E23.filletArc");var subQ11=sQuery(id+"F0.wireOp",EDGE,"E24.filletArc");Q0=makeQuery(id+"F2.boolean.opBoolean","SPLIT",FACE,{"disambiguationData":[TD([makeQuery(id+"F1.opExtrude","SWEPT_FACE",FACE,{"disambiguationData":[OSD([subQ5])]})])],"derivedFrom":makeQuery(id+"F1.opExtrude","CAP_FACE",FACE,{"disambiguationData":[OSD([subQ5,subQ7,subQ8,subQ9,subQ4,subQ3,subQ2,subQ1,subQ6,subQ0,subQ10,subQ11])],"isStart":true})});}
            var sketch = newSketch(context, id + "F16", { "sketchPlane" : qUnion([Q0])});
            skLineSegment(sketch, "E79", {"start": v(-32.87, 90) * mm, "end": v(-14.87, 108) * mm});
            skLineSegment(sketch, "E80", {"start": v(-14.87, 108) * mm, "end": v(-14.87, 120) * mm});
            skLineSegment(sketch, "E81", {"start": v(33.13, 90) * mm, "end": v(15.13, 108) * mm});
            skLineSegment(sketch, "E82", {"start": v(15.13, 108) * mm, "end": v(15.13, 120) * mm});
            skLineSegment(sketch, "E83", {"start": v(0, 90) * mm, "end": v(0, 120) * mm, "construction": true});
            skCircle(sketch, "E84", {"center": v(0, 120) * mm, "radius": 6 * mm});
            skArc(sketch, "E85", {"start": v(15.13, 120) * mm, "mid": v(0.13, 135) * mm, "end": v(-14.87, 120) * mm});
            skLineSegment(sketch, "E86", {"start": v(-80, 0) * mm, "end": v(80, 0) * mm, "construction": true});
            skLineSegment(sketch, "E87.MirrorCS", {"start": v(15.13, -108) * mm, "end": v(15.13, -120) * mm});
            skLineSegment(sketch, "E88.MirrorCS", {"start": v(-32.87, -90) * mm, "end": v(-14.87, -108) * mm});
            skCircle(sketch, "E89.MirrorC", {"center": v(0, -120) * mm, "radius": 6 * mm});
            skLineSegment(sketch, "E90.MirrorCS", {"start": v(0, -90) * mm, "end": v(0, -120) * mm, "construction": true});
            skArc(sketch, "E91.MirrorCS", {"start": v(15.13, -120) * mm, "mid": v(0.13, -135) * mm, "end": v(-14.87, -120) * mm});
            skLineSegment(sketch, "E92.MirrorCS", {"start": v(-14.87, -108) * mm, "end": v(-14.87, -120) * mm});
            skLineSegment(sketch, "E93.MirrorCS", {"start": v(33.13, -90) * mm, "end": v(15.13, -108) * mm});
            skSolve(sketch);
        }
        {
            var Q0;
            {var subQ1=sQuery(id+"F16.wireOp",EDGE,"E79");Q0=makeQuery(id+"F16.imprint","IMPRINT",FACE,{"disambiguationData":[TD([[makeQuery(id+"F16.imprint","IMPRINT",EDGE,{"derivedFrom":subQ1}),-1.0]])]});}
            var Q1;
            Q1=makeQuery(id+"F16.imprint","IMPRINT",FACE,{"disambiguationData":[TD([[makeQuery(id+"F16.imprint","IMPRINT",EDGE,{"derivedFrom":sQuery(id+"F16.wireOp",EDGE,"E87.MirrorCS")}),-1.0]])]});
            var Q2;
            Q2=makeQuery(id+"F16.imprint","IMPRINT",FACE,{"disambiguationData":[TD([[makeQuery(id+"F16.imprint","IMPRINT",EDGE,{"derivedFrom":makeQuery(id+"F1.opExtrude","CAP_EDGE",EDGE,{"disambiguationData":[OSD([sQuery(id+"F0.wireOp",EDGE,"E1.left")])],"isStart":true})}),-1.0]])]});
            var Q3;
            Q3=makeQuery(id+"F2.opExtrude","CAP_FACE",FACE,{"disambiguationData":[OSD([sQuery(id+"F0.wireOp",EDGE,"E12"),sQuery(id+"F0.wireOp",EDGE,"E13"),sQuery(id+"F0.wireOp",EDGE,"E14"),sQuery(id+"F0.wireOp",EDGE,"E15"),sQuery(id+"F0.wireOp",EDGE,"E17.filletArc"),sQuery(id+"F0.wireOp",EDGE,"E18.filletArc"),sQuery(id+"F0.wireOp",EDGE,"E19.filletArc"),sQuery(id+"F0.wireOp",EDGE,"E20.filletArc"),sQuery(id+"F0.wireOp",EDGE,"E25.0"),sQuery(id+"F0.wireOp",EDGE,"E25.1"),sQuery(id+"F0.wireOp",EDGE,"E25.2"),sQuery(id+"F0.wireOp",EDGE,"E25.3"),sQuery(id+"F0.wireOp",EDGE,"E25.4"),sQuery(id+"F0.wireOp",EDGE,"E25.5"),sQuery(id+"F0.wireOp",EDGE,"E25.6"),sQuery(id+"F0.wireOp",EDGE,"E25.7")])],"isStart":false});
            extrude(context, id + "F17", {"entities" : qUnion([Q0, Q1, Q2]), "endBound" : BoundingType.UP_TO_SURFACE, "endBoundEntityFace" : qUnion([Q3]), "depth" : 25 * mm});
        }
    });
